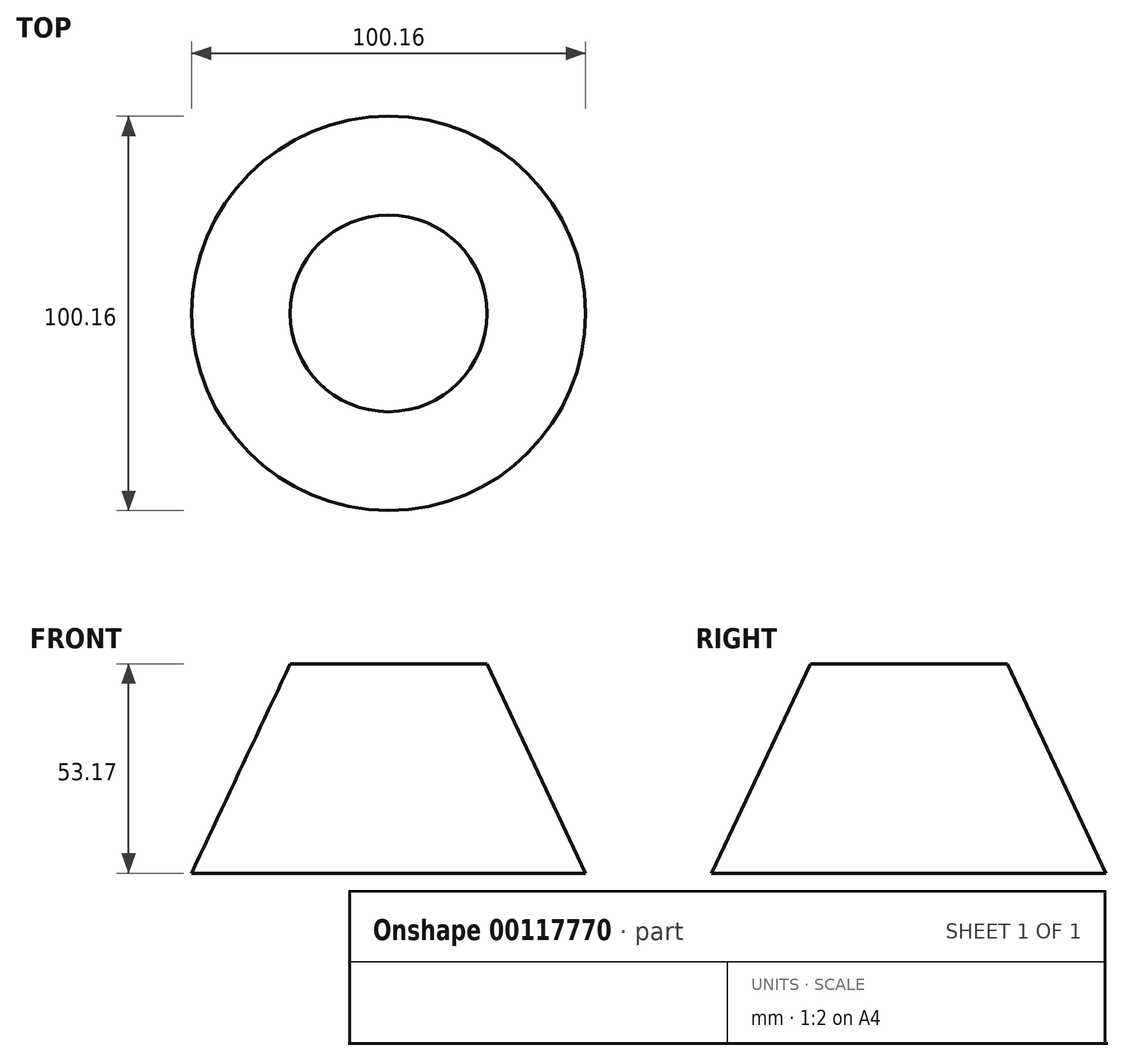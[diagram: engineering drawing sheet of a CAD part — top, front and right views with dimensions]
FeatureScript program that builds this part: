
annotation { "Feature Type Name" : "Feature", "Feature Type Description" : "" }
export const myFeature = defineFeature(function(context is Context, id is Id, definition is map)
    precondition{}
    {
        {
            var Q0;
            Q0=qCreatedBy(makeId("Front.planeOp"),FACE);
            var sketch = newSketch(context, id + "F0", { "sketchPlane" : qUnion([Q0])});
            skLineSegment(sketch, "E0", {"start": v(0, 0) * mm, "end": v(50.08, 0) * mm});
            skLineSegment(sketch, "E1", {"start": v(0, 0) * mm, "end": v(0, 53.17) * mm});
            skLineSegment(sketch, "E2", {"start": v(0, 53.17) * mm, "end": v(25, 53.17) * mm});
            skLineSegment(sketch, "E3", {"start": v(25, 53.17) * mm, "end": v(50.08, 0) * mm});
            skSolve(sketch);
        }
        {
            var Q0;
            Q0=makeQuery(id+"F0.imprint","IMPRINT",FACE,{"disambiguationData":[TD([[makeQuery(id+"F0.imprint","IMPRINT",EDGE,{"derivedFrom":sQuery(id+"F0.wireOp",EDGE,"E0")}),1.0]])]});
            var Q1;
            Q1=sQuery(id+"F0.wireOp",EDGE,"E1");
            revolve(context, id + "F1", {"entities" : qUnion([Q0]), "axis" : qUnion([Q1]), "revolveType" : RevolveType.FULL});
        }
    });
